# Revit family: ELDSSF36279DBG
name_source: partatom
category: Plumbing Fixtures
units: mm (PartAtom-declared; Revit-internal decimal feet)

## family parameters
Always vertical = Yes
Cut with Voids When Loaded = No
OmniClass Number = 23.45.00.00
OmniClass Title = Sanitary, Laundry, and Cleaning Equipment
Part Type = Normal
Room Calculation Point = No
Round Connector Dimension = Use Diameter
Shared = No
Work Plane-Based = No

## types (1)
- ELDSSF36279DBG
    Assembly Code = D2010810
    Bowl 1 Dimensions = 28-7/8inch x 14-7/16inch x 9-5/8inch
    CW Connection = Yes
    Description = Elkay Dart Canyon Stainless Steel Single Bowl Farmhouse ADA Workstation Sink
    Drain Location = Rear Center
    Drain Size = 3-1/2 inch(89mm)
    ELDSSF30279DBG = No
    ELDSSF33279DBG_Visible = No
    ELDSSF36279DBG_Visible = Yes
    Finish = Polished Satin
    Gauge = 16
    HW Connection = No
    Installation Type = Farmhouse
    Manufacturer = Elkay
    Material = 304 Stainless Steel
    Minimum Cabinet Size = 36 inch
    Model = ELDSSF36279DBG
    Mounting Hardware = Part # 54300308 included
    Number of Bowls = 1
    Sink Dimensions = 35-7/8inch x 27-1/4inch x 9-5/8inch
    Sound Deadening = Full spray sides and bottom with Sides and Bottom pads
    Special Features = Work Shelf, Workstation
    Vent Connection = No
    Version = 1.0.0.0
    Waste Connection = Yes

## geometry (parser evidence)
native form markers: Blend x4, Sweep x13
no freeform markers — native parametric forms only
